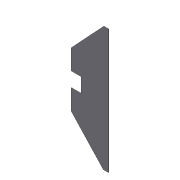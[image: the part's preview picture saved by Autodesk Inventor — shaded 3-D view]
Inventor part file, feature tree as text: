
AUTODESK INVENTOR PART (.ipt)
format: ipt  version: 2012 (Build 160160000, 160)  size: 91,648 bytes
history: native  units: in
note: dims shown in document units (in); Inventor stores cm internally (conversion verified against a paired STEP export)
features: extrude x3, sketch x3
ambient origin geometry x8: Origin, YZ Plane, XZ Plane, XY Plane, X Axis, Y Axis, Z Axis, Center Point
bodies: Solid1 (feature_tree)
feature tree (6):
  extrude  "Extrusion1"  Depth=25.0in
  extrude  "Extrusion2"  Depth=7.0in
  extrude  "Extrusion4"  Depth=7.0in
  sketch  "Sketch1"  dims[d0=7.5in d1=25.0in]
  sketch  "Sketch2"  dims[d2=0.125in d3=0.0in d5=7.0in]
  sketch  "Sketch4"  dims[d6=0.125in d7=0.0in d8=7.0in d9=1.0in d17=3.0in d18=2.0in d19=1.0in d20=0.0in]
